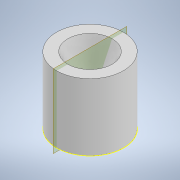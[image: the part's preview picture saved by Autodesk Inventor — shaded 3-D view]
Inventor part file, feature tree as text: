
AUTODESK INVENTOR PART (.ipt)
format: ipt  version: 2020 (Build 240168000, 168)  size: 131,584 bytes
history: native  units: in
note: dims shown in document units (in); Inventor stores cm internally (conversion verified against a paired STEP export)
features: sketch x4, hole x2, revolve x1, plane x1
ambient origin geometry x8: Origin, YZ Plane, XZ Plane, XY Plane, X Axis, Y Axis, Z Axis, Center Point
bodies: Solid1 (feature_tree)
feature tree (8):
  revolve  "Revolution1"  [1 undecoded]
  hole  "Hole1"  [1 undecoded]
  sketch  "Sketch3"  dims[d16=45.0deg d17=90.0deg]
  plane  "Work Plane1"
  hole  "Hole2"  [1 undecoded]
  sketch  "Sketch1"  dims[d7=90.0deg d8=0.211in]
  sketch  "Sketch2"  dims[d10=0.375in d11=0.25in d12=0.5635in d13=0.375in d14=0.8108in d15=0.325in]
  sketch  "Sketch4"  dims[d18=0.4in d19=45.0deg d20=0.4in d21=135.0deg d22=0.177in d23=0.328in d24=0.332in d25=0.25in d26=0.5635in d27=0.484in d28=0.8108in]
note: 3 required parameter values undecoded (feature->parameter linkage not recoverable at this tier; creation-order binding heuristic only, values carry confidence <= 0.55)